# Revit family: ASL_92_Series_wall_starter
name_source: partatom
category: Detail Items
revit_build: Autodesk Revit 2018 (Build: 20170223_1515(x64)
units: mm (PartAtom-declared; Revit-internal decimal feet)

## family parameters
Rotate with component = No
Section Shape = Not Defined
Shared = Yes

## types (4) — shared parameters
Manufacturer = Aluminate Solutions Limited
Technical Info = www.aluminate.nz

## per-type parameters (varying)
| type | Bottom Plate | Steel Track 92mm | Type Comments |
| Skirting 100mm | No | Yes | ASL 92 Series Wall Starter With 100mm Skirting |
| Skirting 120mm | No | Yes | ASL 92 Series Wall Starter With 120mm Skirting |
| Standard | Yes | No | ASL 92 Series Wall Starter Standard |
| Skirting 150mm | No | Yes | ASL 92 Series Wall Starter With 150mm Skirting |

type visibility flags (boolean, named after types; folded from table):
- Skirting 100mm: Yes: Skirting 100mm
- Skirting 120mm: Yes: Skirting 120mm
- Standard: Yes: (none)
- Skirting 150mm: Yes: Skirting 150mm

## geometry (parser evidence)
native form markers: Sweep x7
no freeform markers — native parametric forms only
